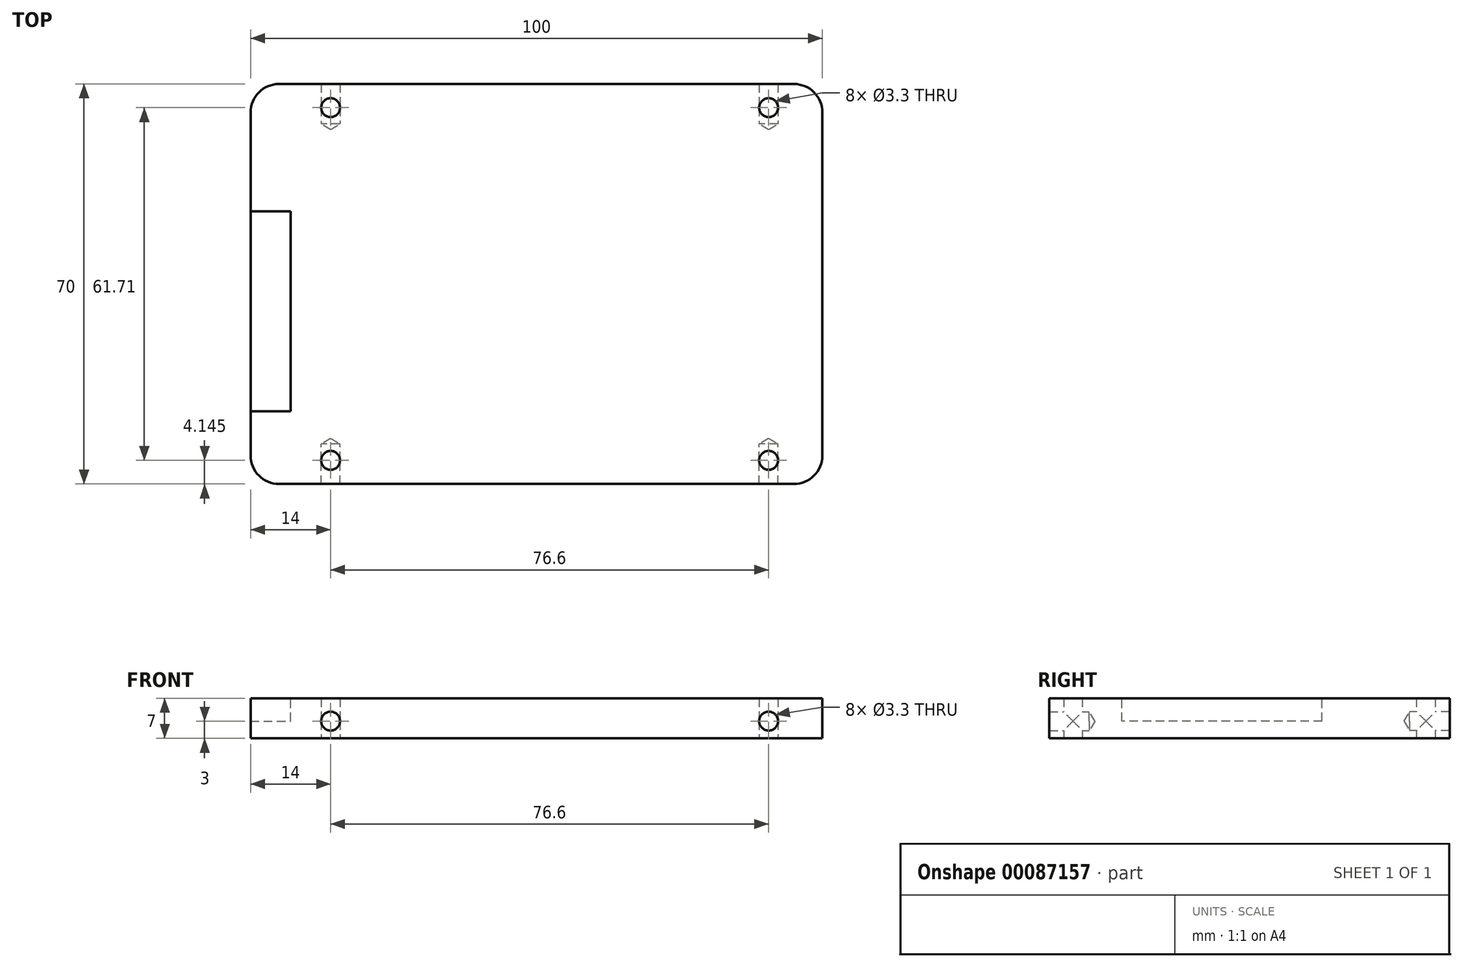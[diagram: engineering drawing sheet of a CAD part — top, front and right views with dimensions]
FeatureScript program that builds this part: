
annotation { "Feature Type Name" : "Feature", "Feature Type Description" : "" }
export const myFeature = defineFeature(function(context is Context, id is Id, definition is map)
    precondition{}
    {
        {
            var Q0;
            Q0=qCreatedBy(makeId("Top.planeOp"),FACE);
            var sketch = newSketch(context, id + "F0", { "sketchPlane" : qUnion([Q0])});
            skLineSegment(sketch, "E0.bottom", {"start": v(-50, 35) * mm, "end": v(50, 35) * mm});
            skLineSegment(sketch, "E0.top", {"start": v(-50, -35) * mm, "end": v(50, -35) * mm});
            skLineSegment(sketch, "E0.left", {"start": v(-50, 35) * mm, "end": v(-50, -35) * mm});
            skLineSegment(sketch, "E0.right", {"start": v(50, 35) * mm, "end": v(50, -35) * mm});
            skSolve(sketch);
        }
        {
            var Q0;
            Q0=makeQuery(id+"F0.imprint","IMPRINT",FACE,{"disambiguationData":[TD([[makeQuery(id+"F0.imprint","IMPRINT",EDGE,{"derivedFrom":sQuery(id+"F0.wireOp",EDGE,"E0.bottom")}),-1.0]])]});
            extrude(context, id + "F1", {"entities" : qUnion([Q0]), "depth" : 7 * mm});
        }
        {
            var Q0;
            Q0=makeQuery(id+"F1.opExtrude","SWEPT_EDGE",EDGE,{"disambiguationData":[OSD([sQuery(id+"F0.wireOp",EDGE,"E0.top"),sQuery(id+"F0.wireOp",EDGE,"E0.left")])]});
            var Q1;
            Q1=makeQuery(id+"F1.opExtrude","SWEPT_EDGE",EDGE,{"disambiguationData":[OSD([sQuery(id+"F0.wireOp",EDGE,"E0.top"),sQuery(id+"F0.wireOp",EDGE,"E0.right")])]});
            var Q2;
            Q2=makeQuery(id+"F1.opExtrude","SWEPT_EDGE",EDGE,{"disambiguationData":[OSD([sQuery(id+"F0.wireOp",EDGE,"E0.bottom"),sQuery(id+"F0.wireOp",EDGE,"E0.left")])]});
            var Q3;
            Q3=makeQuery(id+"F1.opExtrude","SWEPT_EDGE",EDGE,{"disambiguationData":[OSD([sQuery(id+"F0.wireOp",EDGE,"E0.bottom"),sQuery(id+"F0.wireOp",EDGE,"E0.right")])]});
            fillet(context, id + "F2", {"entities" : qUnion([Q0, Q1, Q2, Q3]), "radius" : 5 * mm, "tangentPropagation" : true, "allowEdgeOverflow" : false});
        }
        {
            var Q0;
            Q0=makeQuery(id+"F1.opExtrude","CAP_FACE",FACE,{"disambiguationData":[OSD([sQuery(id+"F0.wireOp",EDGE,"E0.bottom"),sQuery(id+"F0.wireOp",EDGE,"E0.top"),sQuery(id+"F0.wireOp",EDGE,"E0.left"),sQuery(id+"F0.wireOp",EDGE,"E0.right")])],"isStart":false});
            var sketch = newSketch(context, id + "F3", { "sketchPlane" : qUnion([Q0])});
            skPoint(sketch, "E1", {"position": v(-36, 30.86) * mm});
            skPoint(sketch, "E2", {"position": v(40.6, 30.86) * mm});
            skPoint(sketch, "E3", {"position": v(40.6, -30.86) * mm});
            skPoint(sketch, "E4", {"position": v(-36, -30.86) * mm});
            skSolve(sketch);
        }
        {
            var Q0;
            Q0=makeQuery(id+"F1.opExtrude","SWEPT_FACE",FACE,{"disambiguationData":[OSD([sQuery(id+"F0.wireOp",EDGE,"E0.top")])]});
            var sketch = newSketch(context, id + "F4", { "sketchPlane" : qUnion([Q0])});
            skPoint(sketch, "E5", {"position": v(-36, 3) * mm});
            skPoint(sketch, "E6", {"position": v(40.6, 3) * mm});
            skLineSegment(sketch, "E7", {"start": v(-36, 3) * mm, "end": v(-36, 7) * mm, "construction": true});
            skPoint(sketch, "E8.0", {"position": v(-36, 7) * mm});
            skPoint(sketch, "E9.0", {"position": v(40.6, 7) * mm});
            skLineSegment(sketch, "E10", {"start": v(40.6, 3) * mm, "end": v(40.6, 7) * mm, "construction": true});
            skLineSegment(sketch, "E11", {"start": v(-36, 3) * mm, "end": v(40.6, 3) * mm, "construction": true});
            skSolve(sketch);
        }
        {
            var Q0;
            Q0=makeQuery(id+"F1.opExtrude","SWEPT_FACE",FACE,{"disambiguationData":[OSD([sQuery(id+"F0.wireOp",EDGE,"E0.bottom")])]});
            var sketch = newSketch(context, id + "F5", { "sketchPlane" : qUnion([Q0])});
            skPoint(sketch, "E12.0", {"position": v(-40.6, 3) * mm});
            skPoint(sketch, "E12.1", {"position": v(36, 3) * mm});
            skSolve(sketch);
        }
        {
            var Q0;
            Q0=sQuery(id+"F3.wireOp",VERTEX,"E1");
            var Q1;
            Q1=sQuery(id+"F3.wireOp",VERTEX,"E4");
            var Q2;
            Q2=sQuery(id+"F3.wireOp",VERTEX,"E3");
            var Q3;
            Q3=sQuery(id+"F3.wireOp",VERTEX,"E2");
            var Q4;
            Q4=sQuery(id+"F5.wireOp",VERTEX,"E12.0");
            var Q5;
            Q5=sQuery(id+"F4.wireOp",VERTEX,"E5");
            var Q6;
            Q6=sQuery(id+"F4.wireOp",VERTEX,"E6");
            var Q7;
            Q7=sQuery(id+"F5.wireOp",VERTEX,"E12.1");
            var Q8;
            Q8=makeQuery(id+"F1.opExtrude","SWEPT_BODY",BODY,{"disambiguationData":[OSD([sQuery(id+"F0.wireOp",EDGE,"E0.bottom"),sQuery(id+"F0.wireOp",EDGE,"E0.top"),sQuery(id+"F0.wireOp",EDGE,"E0.left"),sQuery(id+"F0.wireOp",EDGE,"E0.right")])]});
            hole(context, id + "F6", {"style" : HoleStyle.SIMPLE, "endStyle" : HoleEndStyle.BLIND, "standardTappedOrClearance" : lookupTablePath({ "standard" : "ISO", "fit" : "Normal", "size" : "M3", "type" : "Clearance" }), "standardBlindInLast" : lookupTablePath({ "fit" : "Standard", "standard" : "ISO", "size" : "M3", "type" : "Clearance" }), "holeDiameter" : 3.3 * mm, "holeDepth" : 7 * mm, "tappedDepth" : 12 * mm, "tapClearance" : 3, "locations" : qUnion([Q0, Q1, Q2, Q3, Q4, Q5, Q6, Q7]), "scope" : qUnion([Q8])});
        }
        {
            var Q0;
            Q0=makeQuery(id+"F1.opExtrude","CAP_FACE",FACE,{"disambiguationData":[OSD([sQuery(id+"F0.wireOp",EDGE,"E0.bottom"),sQuery(id+"F0.wireOp",EDGE,"E0.top"),sQuery(id+"F0.wireOp",EDGE,"E0.left"),sQuery(id+"F0.wireOp",EDGE,"E0.right")])],"isStart":false});
            var sketch = newSketch(context, id + "F7", { "sketchPlane" : qUnion([Q0])});
            skLineSegment(sketch, "E13", {"start": v(-50, 12.7) * mm, "end": v(-43, 12.7) * mm});
            skLineSegment(sketch, "E14", {"start": v(-43, 12.7) * mm, "end": v(-43, -22.3) * mm});
            skLineSegment(sketch, "E15", {"start": v(-43, -22.3) * mm, "end": v(-50, -22.3) * mm});
            skLineSegment(sketch, "E16", {"start": v(-50, -22.3) * mm, "end": v(-50, 12.7) * mm});
            skLineSegment(sketch, "E17", {"start": v(-43, -4.8) * mm, "end": v(-50, -4.8) * mm, "construction": true});
            skSolve(sketch);
        }
        {
            var Q0;
            Q0 = qSketchRegion(id + "F7", true);
            extrude(context, id + "F8", {"entities" : qUnion([Q0]), "operationType" : NewBodyOperationType.REMOVE, "oppositeDirection" : true, "depth" : 4 * mm});
        }
    });
